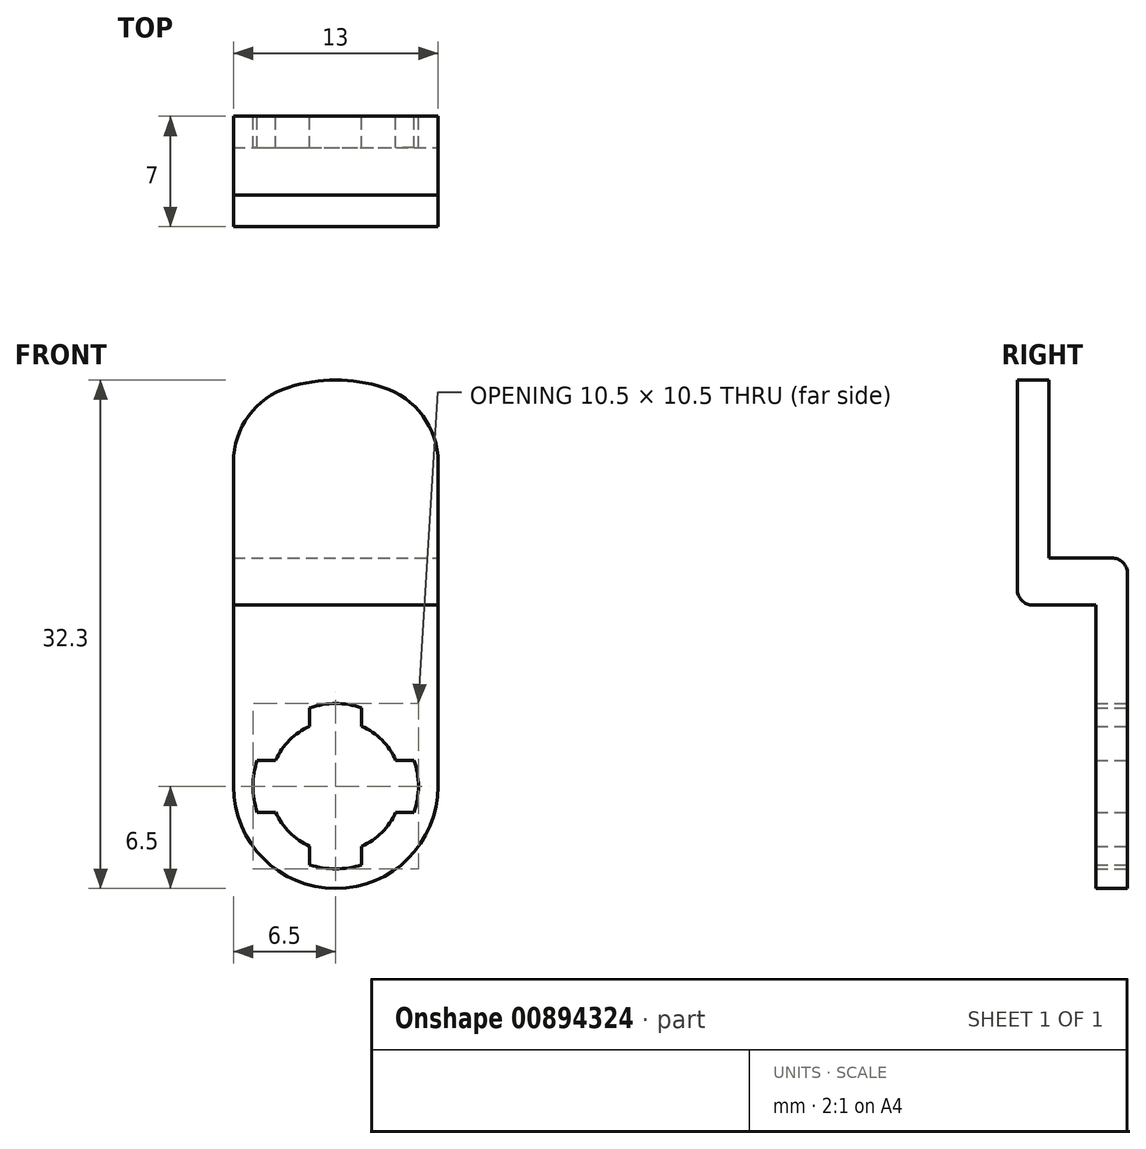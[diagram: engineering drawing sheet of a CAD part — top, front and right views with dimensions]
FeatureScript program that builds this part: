
annotation { "Feature Type Name" : "Feature", "Feature Type Description" : "" }
export const myFeature = defineFeature(function(context is Context, id is Id, definition is map)
    precondition{}
    {
        {
            var Q0;
            Q0=qCreatedBy(makeId("Front.planeOp"),FACE);
            var sketch = newSketch(context, id + "F0", { "sketchPlane" : qUnion([Q0])});
            skCircle(sketch, "E0", {"center": v(0, 0) * mm, "radius": 6.5 * mm});
            skCircle(sketch, "E1", {"center": v(0, 0) * mm, "radius": 5.25 * mm});
            skCircle(sketch, "E2", {"center": v(0, 0) * mm, "radius": 4.15 * mm});
            skLineSegment(sketch, "E3", {"start": v(-1.65, 4.98) * mm, "end": v(-1.65, 3.8) * mm});
            skLineSegment(sketch, "E4.MirrorCS", {"start": v(1.65, 4.98) * mm, "end": v(1.65, 3.8) * mm});
            skLineSegment(sketch, "E5.MirrorCS", {"start": v(-1.65, -4.98) * mm, "end": v(-1.65, -3.8) * mm});
            skLineSegment(sketch, "E6.MirrorCS", {"start": v(1.65, -4.98) * mm, "end": v(1.65, -3.8) * mm});
            skLineSegment(sketch, "E7", {"start": v(0, 0) * mm, "end": v(8.3, 8.3) * mm, "construction": true});
            skLineSegment(sketch, "E8.MirrorCS", {"start": v(4.98, 1.65) * mm, "end": v(3.8, 1.65) * mm});
            skLineSegment(sketch, "E9.MirrorCS", {"start": v(4.98, -1.65) * mm, "end": v(3.8, -1.65) * mm});
            skLineSegment(sketch, "E10.MirrorCS", {"start": v(-4.98, 1.65) * mm, "end": v(-3.8, 1.65) * mm});
            skLineSegment(sketch, "E11.MirrorCS", {"start": v(-4.98, -1.65) * mm, "end": v(-3.8, -1.65) * mm});
            skLineSegment(sketch, "E12.bottom", {"start": v(-6.5, 0) * mm, "end": v(6.5, 0) * mm});
            skLineSegment(sketch, "E12.top", {"start": v(-6.5, 11.5) * mm, "end": v(6.5, 11.5) * mm});
            skLineSegment(sketch, "E12.left", {"start": v(-6.5, 0) * mm, "end": v(-6.5, 11.5) * mm});
            skLineSegment(sketch, "E12.right", {"start": v(6.5, 0) * mm, "end": v(6.5, 11.5) * mm});
            skLineSegment(sketch, "E13.top", {"start": v(-6.5, 23.5) * mm, "end": v(6.5, 23.5) * mm});
            skLineSegment(sketch, "E13.left", {"start": v(-6.5, 0) * mm, "end": v(-6.5, 23.5) * mm});
            skLineSegment(sketch, "E13.right", {"start": v(6.5, 0) * mm, "end": v(6.5, 23.5) * mm});
            skCircle(sketch, "E14", {"center": v(0, 15.8) * mm, "radius": 10 * mm});
            skLineSegment(sketch, "E15", {"start": v(-6.5, 14.5) * mm, "end": v(6.5, 14.5) * mm});
            skSolve(sketch);
        }
        {
            var Q0;
            {var subQ0=sQuery(id+"F0.wireOp",EDGE,"E4.MirrorCS");Q0=makeQuery(id+"F0.imprint","IMPRINT",FACE,{"disambiguationData":[TD([[makeQuery(id+"F0.imprint","IMPRINT",EDGE,{"derivedFrom":subQ0}),1.0]])]});}
            var Q1;
            {var subQ0=sQuery(id+"F0.wireOp",EDGE,"E3");Q1=makeQuery(id+"F0.imprint","IMPRINT",FACE,{"disambiguationData":[TD([[makeQuery(id+"F0.imprint","IMPRINT",EDGE,{"derivedFrom":subQ0}),-1.0]])]});}
            var Q2;
            {var subQ0=sQuery(id+"F0.wireOp",EDGE,"E5.MirrorCS");Q2=makeQuery(id+"F0.imprint","IMPRINT",FACE,{"disambiguationData":[TD([[makeQuery(id+"F0.imprint","IMPRINT",EDGE,{"derivedFrom":subQ0}),1.0]])]});}
            var Q3;
            {var subQ0=sQuery(id+"F0.wireOp",EDGE,"E6.MirrorCS");Q3=makeQuery(id+"F0.imprint","IMPRINT",FACE,{"disambiguationData":[TD([[makeQuery(id+"F0.imprint","IMPRINT",EDGE,{"derivedFrom":subQ0}),-1.0]])]});}
            var Q4;
            {var subQ0=sQuery(id+"F0.wireOp",EDGE,"E1");var subQ8=makeQuery(id+"F0.imprint","INTERSECT",VERTEX,{"derivedFrom":[subQ0,sQuery(id+"F0.wireOp",EDGE,"E6.MirrorCS")]});Q4=makeQuery(id+"F0.imprint","IMPRINT",FACE,{"disambiguationData":[TD([[makeQuery(id+"F0.imprint","IMPRINT",EDGE,{"disambiguationData":[TD([[subQ8,-1.0]])],"derivedFrom":subQ0}),-1.0]])]});}
            var Q5;
            {var subQ0=sQuery(id+"F0.wireOp",EDGE,"E1");var subQ1=makeQuery(id+"F0.imprint","INTERSECT",VERTEX,{"derivedFrom":[subQ0,sQuery(id+"F0.wireOp",EDGE,"E8.MirrorCS")]});Q5=makeQuery(id+"F0.imprint","IMPRINT",FACE,{"disambiguationData":[TD([[makeQuery(id+"F0.imprint","IMPRINT",EDGE,{"disambiguationData":[TD([[subQ1,1.0]])],"derivedFrom":subQ0}),-1.0]])]});}
            var Q6;
            {var subQ0=sQuery(id+"F0.wireOp",EDGE,"E14");var subQ1=sQuery(id+"F0.wireOp",EDGE,"E0");var subQ2=makeQuery(id+"F0.imprint","INTERSECT",VERTEX,{"disambiguationData":[OD(0.0)],"derivedFrom":[subQ1,subQ0]});Q6=makeQuery(id+"F0.imprint","IMPRINT",FACE,{"disambiguationData":[TD([[makeQuery(id+"F0.imprint","IMPRINT",EDGE,{"disambiguationData":[TD([[subQ2,-1.0]])],"derivedFrom":subQ1}),1.0]])]});}
            var Q7;
            {var subQ0=sQuery(id+"F0.wireOp",EDGE,"E12.left");var subQ3=sQuery(id+"F0.wireOp",EDGE,"E14");var subQ5=makeQuery(id+"F0.imprint","INTERSECT",VERTEX,{"derivedFrom":[subQ0,subQ3]});Q7=makeQuery(id+"F0.imprint","IMPRINT",FACE,{"disambiguationData":[TD([[makeQuery(id+"F0.imprint","IMPRINT",EDGE,{"disambiguationData":[TD([[subQ5,-1.0]])],"derivedFrom":subQ3}),-1.0]])]});}
            var Q8;
            {var subQ0=sQuery(id+"F0.wireOp",EDGE,"E12.right");var subQ3=sQuery(id+"F0.wireOp",EDGE,"E14");var subQ5=makeQuery(id+"F0.imprint","INTERSECT",VERTEX,{"derivedFrom":[subQ0,subQ3]});Q8=makeQuery(id+"F0.imprint","IMPRINT",FACE,{"disambiguationData":[TD([[makeQuery(id+"F0.imprint","IMPRINT",EDGE,{"disambiguationData":[TD([[subQ5,1.0]])],"derivedFrom":subQ3}),-1.0]])]});}
            var Q9;
            {var subQ1=sQuery(id+"F0.wireOp",EDGE,"E12.top");Q9=makeQuery(id+"F0.imprint","IMPRINT",FACE,{"disambiguationData":[TD([[makeQuery(id+"F0.imprint","IMPRINT",EDGE,{"derivedFrom":subQ1}),-1.0]])]});}
            extrude(context, id + "F1", {"entities" : qUnion([Q0, Q1, Q2, Q3, Q4, Q5, Q6, Q7, Q8, Q9]), "depth" : 2 * mm, "offsetDistance" : 25 * mm});
        }
        {
            var Q0;
            {var subQ0=sQuery(id+"F0.wireOp",EDGE,"E12.top");Q0=makeQuery(id+"F0.imprint","IMPRINT",FACE,{"disambiguationData":[TD([[makeQuery(id+"F0.imprint","IMPRINT",EDGE,{"derivedFrom":subQ0}),1.0]])]});}
            extrude(context, id + "F2", {"entities" : qUnion([Q0]), "operationType" : NewBodyOperationType.ADD, "depth" : 7 * mm, "offsetDistance" : 25 * mm});
        }
        {
            var Q0;
            {var subQ6=sQuery(id+"F0.wireOp",EDGE,"E15");Q0=makeQuery(id+"F0.imprint","IMPRINT",FACE,{"disambiguationData":[TD([[makeQuery(id+"F0.imprint","IMPRINT",EDGE,{"derivedFrom":subQ6}),1.0]])]});}
            var Q1;
            {var subQ0=sQuery(id+"F0.wireOp",EDGE,"E14");var subQ1=sQuery(id+"F0.wireOp",EDGE,"E13.top");var subQ2=makeQuery(id+"F0.imprint","INTERSECT",VERTEX,{"disambiguationData":[OD(0.0)],"derivedFrom":[subQ1,subQ0]});Q1=makeQuery(id+"F0.imprint","IMPRINT",FACE,{"disambiguationData":[TD([[makeQuery(id+"F0.imprint","IMPRINT",EDGE,{"disambiguationData":[TD([[subQ2,-1.0]])],"derivedFrom":subQ1}),1.0]])]});}
            var Q2;
            Q2=makeQuery(id+"F1.opExtrude","SWEPT_BODY",BODY,{"disambiguationData":[OSD([sQuery(id+"F0.wireOp",EDGE,"E0"),sQuery(id+"F0.wireOp",EDGE,"E1"),sQuery(id+"F0.wireOp",EDGE,"E2"),sQuery(id+"F0.wireOp",EDGE,"E3"),sQuery(id+"F0.wireOp",EDGE,"E4.MirrorCS"),sQuery(id+"F0.wireOp",EDGE,"E5.MirrorCS"),sQuery(id+"F0.wireOp",EDGE,"E6.MirrorCS"),sQuery(id+"F0.wireOp",EDGE,"E8.MirrorCS"),sQuery(id+"F0.wireOp",EDGE,"E9.MirrorCS"),sQuery(id+"F0.wireOp",EDGE,"E10.MirrorCS"),sQuery(id+"F0.wireOp",EDGE,"E11.MirrorCS"),sQuery(id+"F0.wireOp",EDGE,"E12.top"),sQuery(id+"F0.wireOp",EDGE,"E12.left"),sQuery(id+"F0.wireOp",EDGE,"E12.right")])]});
            extrude(context, id + "F3", {"entities" : qUnion([Q0, Q1]), "operationType" : NewBodyOperationType.ADD, "depth" : 7 * mm, "offsetDistance" : 25 * mm, "hasSecondDirection" : true, "secondDirectionOppositeDirection" : false, "secondDirectionDepth" : 5 * mm, "secondDirectionBoundEntityBody" : qUnion([Q2])});
        }
        {
            var Q0;
            Q0=makeQuery(id+"F1.opExtrude","CAP_EDGE",EDGE,{"disambiguationData":[OSD([sQuery(id+"F0.wireOp",EDGE,"E12.top")])],"isStart":false});
            var Q1;
            Q1=makeQuery(id+"F2.opExtrude","CAP_EDGE",EDGE,{"disambiguationData":[OSD([sQuery(id+"F0.wireOp",EDGE,"E12.top")])],"isStart":false});
            var Q2;
            Q2=makeQuery(id+"F2.opExtrude","CAP_EDGE",EDGE,{"disambiguationData":[OSD([sQuery(id+"F0.wireOp",EDGE,"E15")])],"isStart":true});
            var Q3;
            Q3=makeQuery(id+"F3.opExtrude","CAP_EDGE",EDGE,{"disambiguationData":[OSD([sQuery(id+"F0.wireOp",EDGE,"E15")])],"isStart":true});
            fillet(context, id + "F4", {"entities" : qUnion([Q0, Q1, Q2, Q3]), "radius" : 1 * mm, "tangentPropagation" : true, "allowEdgeOverflow" : false});
        }
        {
            var Q0;
            Q0=makeQuery(id+"F3.opExtrude","SWEPT_EDGE",EDGE,{"disambiguationData":[OSD([sQuery(id+"F0.wireOp",EDGE,"E13.right"),sQuery(id+"F0.wireOp",EDGE,"E14")])]});
            var Q1;
            Q1=makeQuery(id+"F3.opExtrude","SWEPT_EDGE",EDGE,{"disambiguationData":[OSD([sQuery(id+"F0.wireOp",EDGE,"E13.left"),sQuery(id+"F0.wireOp",EDGE,"E14")])]});
            fillet(context, id + "F5", {"entities" : qUnion([Q0, Q1]), "radius" : 5 * mm, "tangentPropagation" : true, "allowEdgeOverflow" : false});
        }
    });
